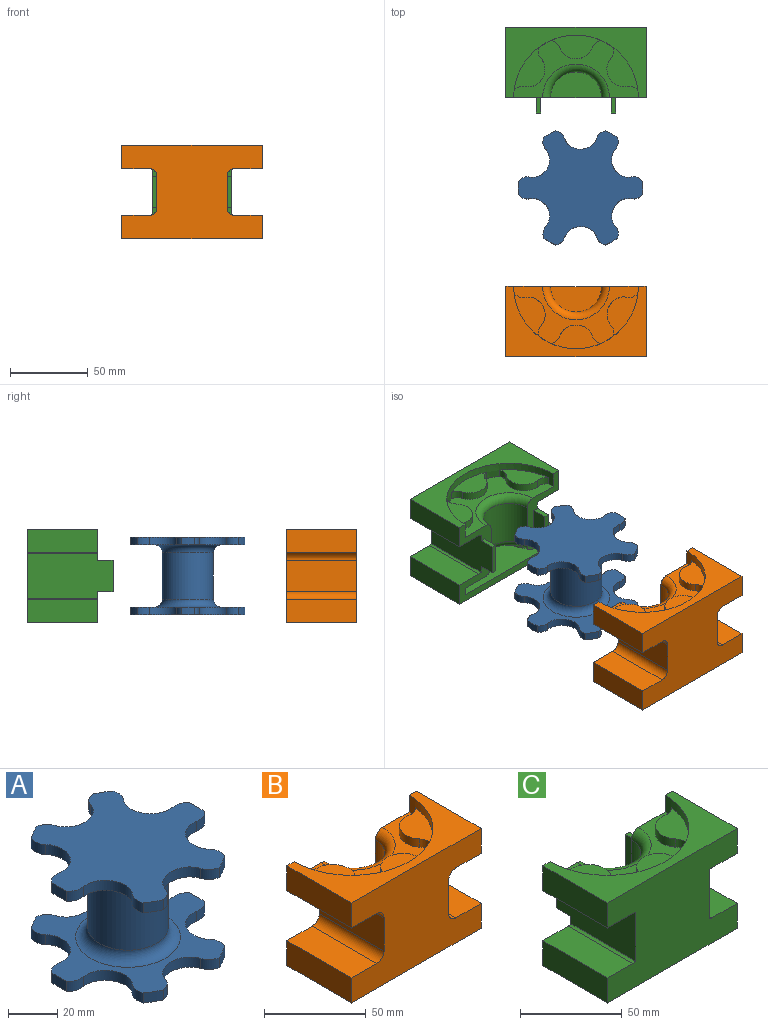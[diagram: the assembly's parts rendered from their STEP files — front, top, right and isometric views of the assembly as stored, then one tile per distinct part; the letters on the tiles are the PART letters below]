
ASSEMBLY  parts=3 mates=3
PART A: 55 faces, bbox 80x73.2x50 mm
  f0: cylinder r=40mm len=8.67mm, axis (0,0,-1), area 43.5mm2, adj f11,f12,f38,f52
  f1: cylinder r=40mm len=7.52mm, axis (0,0,-1), area 43.5mm2, adj f11,f12,f49,f53
  f2: cylinder r=40mm len=7.51mm, axis (0,0,-1), area 43.5mm2, adj f11,f12,f46,f50
  f3: cylinder r=40mm len=8.67mm, axis (0,0,-1), area 43.5mm2, adj f11,f12,f43,f47
  f4: cylinder r=40mm len=7.52mm, axis (0,0,-1), area 43.5mm2, adj f11,f12,f40,f44
  f5: cylinder r=40mm len=7.51mm, axis (0,0,-1), area 43.5mm2, adj f11,f12,f37,f41
  f6: cylinder r=40mm len=7.52mm, axis (0,0,-1), area 43.5mm2, adj f13,f14,f33,f35
  f7: cylinder r=40mm len=7.51mm, axis (0,0,-1), area 43.5mm2, adj f13,f14,f30,f32
  f8: cylinder r=40mm len=8.67mm, axis (0,0,-1), area 43.5mm2, adj f13,f14,f27,f29
  f9: cylinder r=40mm len=7.52mm, axis (0,0,-1), area 43.5mm2, adj f13,f14,f24,f26
  f10: cylinder r=40mm len=7.51mm, axis (0,0,-1), area 43.5mm2, adj f13,f14,f21,f23
  f11: plane 80x73.23mm, normal (0,0,-1), area 3247.5mm2, adj f0,f1,f2,f3,f4,f5,f37,f38
  f12: plane 80x73.23mm, normal (0,0,1), area 1808.8mm2, adj f0,f1,f2,f3,f4,f5,f15,f37
  f13: plane 80x73.23mm, normal (0,0,-1), area 1808.8mm2, adj f6,f7,f8,f9,f10,f17,f18,f19
  f14: plane 80x73.23mm, normal (0,0,1), area 3247.5mm2, adj f6,f7,f8,f9,f10,f18,f19,f20
  f15: torus R=21.4mm, axis (0,0,-1), area 899mm2, adj f12,f16
  f16: cylinder r=16.4mm len=32.8mm, axis (0,0,-1), area 3091.3mm2, adj f15,f17
  f17: torus R=21.4mm, axis (0,0,-1), area 899mm2, adj f13,f16
  f18: cylinder r=40mm len=8.67mm, axis (0,0,-1), area 43.5mm2, adj f13,f14,f20,f36
  f19: extruded ~18.18x12.74mm, area 133.7mm2, adj f13,f14,f20,f21
  f20: cylinder r=7.1mm len=7.1mm, axis (0,0,1), area 39.9mm2, adj f13,f14,f18,f19
  f21: cylinder r=7.1mm len=7.34mm, axis (0,0,1), area 39.2mm2, adj f10,f13,f14,f19
  f22: extruded ~20.68x7.13mm, area 133.7mm2, adj f13,f14,f23,f24
  f23: cylinder r=7.1mm len=5.81mm, axis (0,0,1), area 39.9mm2, adj f10,f13,f14,f22
  f24: cylinder r=7.1mm len=5.76mm, axis (0,0,1), area 39.2mm2, adj f9,f13,f14,f22
  f25: extruded ~18.03x12.94mm, area 133.7mm2, adj f13,f14,f26,f27
  f26: cylinder r=7.1mm len=7.46mm, axis (0,0,1), area 39.9mm2, adj f9,f13,f14,f25
  f27: cylinder r=7.1mm len=6.96mm, axis (0,0,1), area 39.2mm2, adj f8,f13,f14,f25
  f28: extruded ~18.18x12.74mm, area 133.7mm2, adj f13,f14,f29,f30
  f29: cylinder r=7.1mm len=7.1mm, axis (0,0,1), area 39.9mm2, adj f8,f13,f14,f28
  f30: cylinder r=7.1mm len=7.34mm, axis (0,0,1), area 39.2mm2, adj f7,f13,f14,f28
  f31: extruded ~20.68x7.13mm, area 133.7mm2, adj f13,f14,f32,f33
  f32: cylinder r=7.1mm len=5.81mm, axis (0,0,1), area 39.9mm2, adj f7,f13,f14,f31
  f33: cylinder r=7.1mm len=5.76mm, axis (0,0,1), area 39.2mm2, adj f6,f13,f14,f31
  f34: extruded ~18.03x12.94mm, area 133.7mm2, adj f13,f14,f35,f36
  f35: cylinder r=7.1mm len=7.46mm, axis (0,0,1), area 39.9mm2, adj f6,f13,f14,f34
  f36: cylinder r=7.1mm len=6.96mm, axis (0,0,1), area 39.2mm2, adj f13,f14,f18,f34
  f37: cylinder r=7.1mm len=7.34mm, axis (0,0,1), area 39.2mm2, adj f5,f11,f12,f39
  f38: cylinder r=7.1mm len=7.1mm, axis (0,0,1), area 39.9mm2, adj f0,f11,f12,f39
  f39: extruded ~18.18x12.74mm, area 133.7mm2, adj f11,f12,f37,f38
  f40: cylinder r=7.1mm len=5.76mm, axis (0,0,1), area 39.2mm2, adj f4,f11,f12,f42
  f41: cylinder r=7.1mm len=5.81mm, axis (0,0,1), area 39.9mm2, adj f5,f11,f12,f42
  f42: extruded ~20.68x7.13mm, area 133.7mm2, adj f11,f12,f40,f41
  f43: cylinder r=7.1mm len=6.96mm, axis (0,0,1), area 39.2mm2, adj f3,f11,f12,f45
  f44: cylinder r=7.1mm len=7.46mm, axis (0,0,1), area 39.9mm2, adj f4,f11,f12,f45
  f45: extruded ~18.03x12.94mm, area 133.7mm2, adj f11,f12,f43,f44
  f46: cylinder r=7.1mm len=7.34mm, axis (0,0,1), area 39.2mm2, adj f2,f11,f12,f48
  f47: cylinder r=7.1mm len=7.1mm, axis (0,0,1), area 39.9mm2, adj f3,f11,f12,f48
  f48: extruded ~18.18x12.74mm, area 133.7mm2, adj f11,f12,f46,f47
  f49: cylinder r=7.1mm len=5.76mm, axis (0,0,1), area 39.2mm2, adj f1,f11,f12,f51
  f50: cylinder r=7.1mm len=5.81mm, axis (0,0,1), area 39.9mm2, adj f2,f11,f12,f51
  f51: extruded ~20.68x7.13mm, area 133.7mm2, adj f11,f12,f49,f50
  f52: cylinder r=7.1mm len=6.96mm, axis (0,0,1), area 39.2mm2, adj f0,f11,f12,f54
  f53: cylinder r=7.1mm len=7.46mm, axis (0,0,1), area 39.9mm2, adj f1,f11,f12,f54
  f54: extruded ~18.03x12.94mm, area 133.7mm2, adj f11,f12,f52,f53
PART B: 50 faces, bbox 90x45x60.1 mm
  f0: plane 90x45mm, normal (0,0,1), area 1536.7mm2, adj f20,f21,f25,f26,f29
  f1: extruded ~18.18x12.74mm, area 132.6mm2, adj f2,f3,f32,f47
  f2: cylinder r=7.1mm len=7.1mm, axis (0,0,1), area 39.6mm2, adj f1,f29,f32,f47
  f3: cylinder r=7.1mm len=7.34mm, axis (0,0,1), area 38.8mm2, adj f1,f29,f32,f47
  f4: extruded ~20.68x7.13mm, area 132.6mm2, adj f5,f6,f32,f48
  f5: cylinder r=7.1mm len=5.81mm, axis (0,0,1), area 39.6mm2, adj f4,f29,f32,f48
  f6: cylinder r=7.1mm len=5.76mm, axis (0,0,1), area 38.8mm2, adj f4,f29,f32,f48
  f7: extruded ~18.03x12.94mm, area 132.6mm2, adj f8,f9,f32,f49
  f8: cylinder r=7.1mm len=7.46mm, axis (0,0,1), area 39.6mm2, adj f7,f29,f32,f49
  f9: cylinder r=7.1mm len=6.96mm, axis (0,0,1), area 38.8mm2, adj f7,f29,f32,f49
  f10: cylinder r=5mm len=45mm, axis (0,1,0), area 353.4mm2, adj f11,f24,f25,f26
  f11: plane 45x17.5mm, normal (0,0,1), area 787.5mm2, adj f10,f12,f25,f26
  f12: plane 45x15mm, normal (-1,0,0), area 675mm2, adj f11,f13,f25,f26
  f13: plane 90x45mm, normal (0,0,-1), area 4050mm2, adj f12,f14,f25,f26
  f14: plane 45x15mm, normal (1,0,0), area 675mm2, adj f13,f15,f25,f26
  f15: plane 45x17.5mm, normal (0,0,1), area 787.5mm2, adj f14,f16,f25,f26
  f16: cylinder r=5mm len=45mm, axis (0,1,0), area 353.4mm2, adj f15,f17,f25,f26
  f17: plane 45x20.12mm, normal (1,0,0), area 905.3mm2, adj f16,f18,f25,f26
  f18: cylinder r=5mm len=45mm, axis (0,1,0), area 353.4mm2, adj f17,f19,f25,f26
  f19: plane 45x17.5mm, normal (0,0,-1), area 787.5mm2, adj f18,f20,f25,f26
  f20: plane 45x15mm, normal (1,0,0), area 675mm2, adj f0,f19,f25,f26
  f21: plane 45x15mm, normal (-1,0,0), area 675mm2, adj f0,f22,f25,f26
  f22: plane 45x17.5mm, normal (0,0,-1), area 787.5mm2, adj f21,f23,f25,f26
  f23: cylinder r=5mm len=45mm, axis (0,1,0), area 353.4mm2, adj f22,f24,f25,f26
  f24: plane 45x20.12mm, normal (-1,0,0), area 905.3mm2, adj f10,f23,f25,f26
  f25: plane 90x60.12mm, normal (0,-1,0), area 4076.7mm2, adj f0,f10,f11,f12,f13,f14,f15,f16
  f26: plane 90x60.12mm, normal (0,1,0), area 1538.6mm2, adj f0,f10,f11,f12,f13,f14,f15,f16
  f27: cylinder r=40mm len=5mm, axis (0,0,-1), area 21.6mm2, adj f26,f30,f31,f39
  f28: cylinder r=40mm len=5mm, axis (0,0,-1), area 21.9mm2, adj f26,f30,f31,f44
  f29: cylinder r=40mm len=80mm, axis (0,0,-1), area 770.2mm2, adj f0,f2,f3,f5,f6,f8,f9,f26
  f30: plane 80x36.62mm, normal (0,0,1), area 1623.7mm2, adj f26,f27,f28,f36,f37,f38,f39,f40
  f31: plane 80x36.62mm, normal (0,0,-1), area 904.4mm2, adj f26,f27,f28,f33,f36,f37,f38,f39
  f32: plane 80x36.62mm, normal (0,0,1), area 904.4mm2, adj f1,f2,f3,f4,f5,f6,f7,f8
  f33: torus R=21.4mm, axis (0,0,-1), area 449.5mm2, adj f26,f31,f34
  f34: cylinder r=16.4mm len=32.8mm, axis (0,0,-1), area 1545.7mm2, adj f26,f33,f35
  f35: torus R=21.4mm, axis (0,0,-1), area 449.5mm2, adj f26,f32,f34
  f36: cylinder r=40mm len=7.52mm, axis (0,0,-1), area 43.5mm2, adj f30,f31,f41,f45
  f37: cylinder r=40mm len=7.51mm, axis (0,0,-1), area 43.5mm2, adj f30,f31,f38,f42
  f38: cylinder r=7.1mm len=7.34mm, axis (0,0,1), area 39.2mm2, adj f30,f31,f37,f40
  f39: cylinder r=7.1mm len=7.1mm, axis (0,0,1), area 39.9mm2, adj f27,f30,f31,f40
  f40: extruded ~18.18x12.74mm, area 133.7mm2, adj f30,f31,f38,f39
  f41: cylinder r=7.1mm len=5.76mm, axis (0,0,1), area 39.2mm2, adj f30,f31,f36,f43
  f42: cylinder r=7.1mm len=5.81mm, axis (0,0,1), area 39.9mm2, adj f30,f31,f37,f43
  f43: extruded ~20.68x7.13mm, area 133.7mm2, adj f30,f31,f41,f42
  f44: cylinder r=7.1mm len=6.96mm, axis (0,0,1), area 39.2mm2, adj f28,f30,f31,f46
  f45: cylinder r=7.1mm len=7.46mm, axis (0,0,1), area 39.9mm2, adj f30,f31,f36,f46
  f46: extruded ~18.03x12.94mm, area 133.7mm2, adj f30,f31,f44,f45
  f47: plane 27.94x19.84mm, normal (0,0,1), area 296.5mm2, adj f1,f2,f3,f29
  f48: plane 32.25x15.23mm, normal (0,0,1), area 296.5mm2, adj f4,f5,f6,f29
  f49: plane 27.92x19.9mm, normal (0,0,1), area 296.5mm2, adj f7,f8,f9,f29
PART C: 58 faces, bbox 90x55x60.1 mm
  f0: cylinder r=5mm len=45mm, axis (0,1,0), area 92.6mm2, adj f19,f25,f26,f57
  f1: cylinder r=5mm len=45mm, axis (0,1,0), area 92.6mm2, adj f20,f25,f26,f57
  f2: plane 10x3mm, normal (0,0,1), area 30mm2, adj f26,f50,f51,f52
  f3: plane 10x3mm, normal (0,0,-1), area 30mm2, adj f26,f50,f51,f52
  f4: plane 90x45mm, normal (0,0,1), area 1536.7mm2, adj f21,f22,f25,f26,f29
  f5: extruded ~18.18x12.74mm, area 132.6mm2, adj f6,f7,f32,f47
  f6: cylinder r=7.1mm len=7.1mm, axis (0,0,1), area 39.6mm2, adj f5,f29,f32,f47
  f7: cylinder r=7.1mm len=7.34mm, axis (0,0,1), area 38.8mm2, adj f5,f29,f32,f47
  f8: extruded ~20.68x7.13mm, area 132.6mm2, adj f9,f10,f32,f48
  f9: cylinder r=7.1mm len=5.81mm, axis (0,0,1), area 39.6mm2, adj f8,f29,f32,f48
  f10: cylinder r=7.1mm len=5.76mm, axis (0,0,1), area 38.8mm2, adj f8,f29,f32,f48
  f11: extruded ~18.03x12.94mm, area 132.6mm2, adj f12,f13,f32,f49
  f12: cylinder r=7.1mm len=7.46mm, axis (0,0,1), area 39.6mm2, adj f11,f29,f32,f49
  f13: cylinder r=7.1mm len=6.96mm, axis (0,0,1), area 38.8mm2, adj f11,f29,f32,f49
  f14: cylinder r=5mm len=45mm, axis (0,1,0), area 92.6mm2, adj f15,f25,f26,f52
  f15: plane 45x17.5mm, normal (0,0,1), area 787.5mm2, adj f14,f16,f25,f26
  f16: plane 45x15mm, normal (-1,0,0), area 675mm2, adj f15,f17,f25,f26
  f17: plane 90x45mm, normal (0,0,-1), area 4050mm2, adj f16,f18,f25,f26
  f18: plane 45x15mm, normal (1,0,0), area 675mm2, adj f17,f19,f25,f26
  f19: plane 45x17.5mm, normal (0,0,1), area 787.5mm2, adj f0,f18,f25,f26
  f20: plane 45x17.5mm, normal (0,0,-1), area 787.5mm2, adj f1,f21,f25,f26
  f21: plane 45x15mm, normal (1,0,0), area 675mm2, adj f4,f20,f25,f26
  f22: plane 45x15mm, normal (-1,0,0), area 675mm2, adj f4,f23,f25,f26
  f23: plane 45x17.5mm, normal (0,0,-1), area 787.5mm2, adj f22,f24,f25,f26
  f24: cylinder r=5mm len=45mm, axis (0,1,0), area 92.6mm2, adj f23,f25,f26,f52
  f25: plane 90x60.12mm, normal (0,-1,0), area 4237.1mm2, adj f0,f1,f4,f14,f15,f16,f17,f18
  f26: plane 90x60.12mm, normal (0,1,0), area 1578.2mm2, adj f0,f1,f2,f3,f4,f14,f15,f16
  f27: cylinder r=40mm len=5mm, axis (0,0,-1), area 21.6mm2, adj f26,f30,f31,f39
  f28: cylinder r=40mm len=5mm, axis (0,0,-1), area 21.9mm2, adj f26,f30,f31,f44
  f29: cylinder r=40mm len=80mm, axis (0,0,-1), area 770.2mm2, adj f4,f6,f7,f9,f10,f12,f13,f26
  f30: plane 80x36.62mm, normal (0,0,1), area 1623.7mm2, adj f26,f27,f28,f36,f37,f38,f39,f40
  f31: plane 80x36.62mm, normal (0,0,-1), area 904.4mm2, adj f26,f27,f28,f33,f36,f37,f38,f39
  f32: plane 80x36.62mm, normal (0,0,1), area 904.4mm2, adj f5,f6,f7,f8,f9,f10,f11,f12
  f33: torus R=21.4mm, axis (0,0,-1), area 449.5mm2, adj f26,f31,f34
  f34: cylinder r=16.4mm len=32.8mm, axis (0,0,-1), area 1545.7mm2, adj f26,f33,f35
  f35: torus R=21.4mm, axis (0,0,-1), area 449.5mm2, adj f26,f32,f34
  f36: cylinder r=40mm len=7.52mm, axis (0,0,-1), area 43.5mm2, adj f30,f31,f41,f45
  f37: cylinder r=40mm len=7.51mm, axis (0,0,-1), area 43.5mm2, adj f30,f31,f38,f42
  f38: cylinder r=7.1mm len=7.34mm, axis (0,0,1), area 39.2mm2, adj f30,f31,f37,f40
  f39: cylinder r=7.1mm len=7.1mm, axis (0,0,1), area 39.9mm2, adj f27,f30,f31,f40
  f40: extruded ~18.18x12.74mm, area 133.7mm2, adj f30,f31,f38,f39
  f41: cylinder r=7.1mm len=5.76mm, axis (0,0,1), area 39.2mm2, adj f30,f31,f36,f43
  f42: cylinder r=7.1mm len=5.81mm, axis (0,0,1), area 39.9mm2, adj f30,f31,f37,f43
  f43: extruded ~20.68x7.13mm, area 133.7mm2, adj f30,f31,f41,f42
  f44: cylinder r=7.1mm len=6.96mm, axis (0,0,1), area 39.2mm2, adj f28,f30,f31,f46
  f45: cylinder r=7.1mm len=7.46mm, axis (0,0,1), area 39.9mm2, adj f30,f31,f36,f46
  f46: extruded ~18.03x12.94mm, area 133.7mm2, adj f30,f31,f44,f45
  f47: plane 27.94x19.84mm, normal (0,0,1), area 296.5mm2, adj f5,f6,f7,f29
  f48: plane 32.25x15.23mm, normal (0,0,1), area 296.5mm2, adj f8,f9,f10,f29
  f49: plane 27.92x19.9mm, normal (0,0,1), area 296.5mm2, adj f11,f12,f13,f29
  f50: plane 20.12x10mm, normal (1,0,0), area 201.2mm2, adj f2,f3,f26,f51
  f51: plane 20.12x3mm, normal (0,1,0), area 60.4mm2, adj f2,f3,f50,f52
  f52: plane 55x29.28mm, normal (-1,0,0), area 1518.9mm2, adj f2,f3,f14,f24,f25,f26,f51
  f53: plane 20.12x10mm, normal (-1,0,0), area 201.2mm2, adj f26,f54,f55,f56
  f54: plane 10x3mm, normal (0,0,-1), area 30mm2, adj f26,f53,f55,f57
  f55: plane 20.12x3mm, normal (0,1,0), area 60.4mm2, adj f53,f54,f56,f57
  f56: plane 10x3mm, normal (0,0,1), area 30mm2, adj f26,f53,f55,f57
  f57: plane 55x29.28mm, normal (1,0,0), area 1518.9mm2, adj f0,f1,f25,f26,f54,f55,f56
PLACE A t=(89.75,-88.61,-9.94)mm
PLACE B t=(86.8,-151.88,-9.94)mm
PLACE C rot(axis=(0,0,1),180deg) t=(86.8,-30.55,-9.94)mm fixed
MATE planar C.f17 <-> B.f13  axis (0,0,-1) through (86.8,-8.05,-39.99)mm
MATE planar A.f0 <-> B.f30  axis (0,0,-1) through (89.75,-88.61,-34.94)mm
MATE planar C.f21 <-> B.f21  axis (-1,0,0) through (41.8,-8.05,12.62)mm
